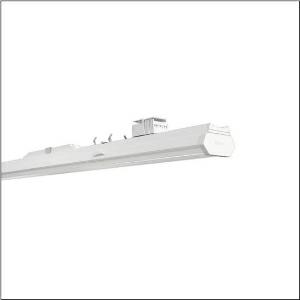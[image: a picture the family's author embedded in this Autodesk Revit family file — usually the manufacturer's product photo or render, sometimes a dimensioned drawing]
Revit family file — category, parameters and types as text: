
# Revit family: licross_r__21_protected_ho_52td12dn4e5m3c_ce33
name_source: partatom
category: Lighting Fixtures
units: mm (PartAtom-declared; Revit-internal decimal feet)

## family parameters
Cut with Voids When Loaded = No
Host = Face
Light Source = No
Part Type = Normal
Room Calculation Point = No
Round Connector Dimension = Use Diameter
Shared = No

## types (1)
- --- (1 x LED, 910 lm, 7.6 W, 4000K)
    Apparent Load = 8 VA
    CIE Flux Codes = 70 91 97 98 100
    Color Rendering = 80
    Color Temperature = 4000K
    Default Elevation = 1800 mm
    Description = Licross® 21 Protected HO, luminaire insert, of sheet steel, galvanised, coil coated, white, length: 1.500mm, width: 90mm, height: 103mm, LED rated luminous flux: 14.690lm, light colour: 840, control gear: DALI 2 (for two DALI lines), with plug, 6-pole, with phase selection, for trunking rail, 14-core, mains connection: 220..240V, AC, 50/60Hz, rated input power: 89W, for trunking rail, 14-core, internal wiring halogen-free, for emergency light function, converter,control gear: single battery element, battery: LiFePO4, 9Ah, primary light control with lens, of plastic, primary optical cover: cover, of PMMA, light emission: direct distribution, primary light characteristic: symmetric, protection rating (complete): IP54, insulation class (complete): insulation class I (protective earthing), certification: CE, UKCA, protection symbol: D if used in an environment with non-conductive dust loads with corresponding accessories, impact resistance: IK06, permissible ambient temperature for indoor applications: +5..+30°C, standard: EN 60598-2-22, LABS conformity tested according to VDMA 24364:2018-05, reducing of maximum allowable ambient temperature of 5°C with ceiling mounting, corresponds to IFS (International Featured Standards) requirements for safety and quality in the food industry, packaging unit: 1 piece
    Height = 92 mm
    Lamp = 1 x LED
    Lamp Light Flux = 910 lm
    Lamp Power = 7.6 W
    Lamp count = 1
    Length = 1500 mm
    Luminous efficacy = 120 lm/W
    Manufacturer = Siteco
    ModVariant = No
    Model = 52TD12DN4E5M3C
    Mounting Place = Ceiling
    Mounting Type = Pendant
    Number of Poles = 1
    OnlyDefault = Yes
    Power Factor = 1
    Product Name = Licross® 21 Protected HO
    Product group = luminaire insert | ceiling pendant
    ProductGroupID = 902
    Protection Class = Protection class I
    Protection Degree = IP 54
    RLX_Detail_Level = 1
    RLX_Emergency_Light_Flux = 0 lm
    RLX_Emergency_Type = 0
    RLX_Emergency_Type_DB = No
    RlxData = <blob elided: 25001 chars, md5=39c2842e>
    Socket = socket
    Standby Power = 0 W
    System Light Flux = 910 lm
    System Power = 8 W
    Type Comments = : emergency light operation: 3 h
    Type Image = l_1256148.jpg
    URL = http://relux.com
    VarID = @adj_132705
    Voltage = 0 V
    Weight = 0.00 kg
    Width = 88 mm

## geometry (parser evidence)
native form markers: Blend x4, Sweep x8
no freeform markers — native parametric forms only
